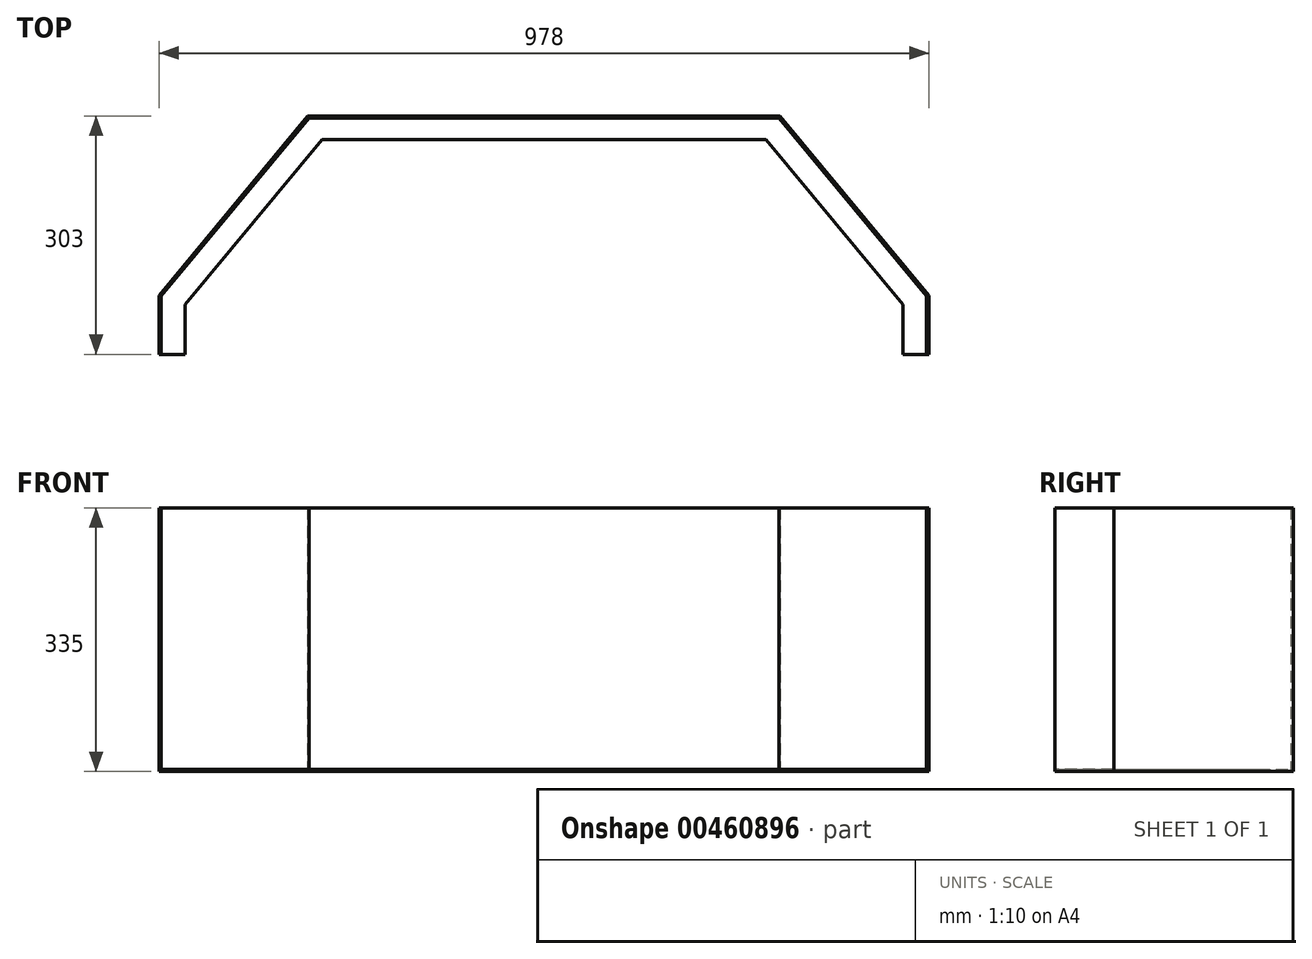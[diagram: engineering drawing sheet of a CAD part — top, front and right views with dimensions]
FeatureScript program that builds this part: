
annotation { "Feature Type Name" : "Feature", "Feature Type Description" : "" }
export const myFeature = defineFeature(function(context is Context, id is Id, definition is map)
    precondition{}
    {
        {
            var Q0;
            Q0=qCreatedBy(makeId("Top.planeOp"),FACE);
            var sketch = newSketch(context, id + "F0", { "sketchPlane" : qUnion([Q0])});
            skLineSegment(sketch, "E0", {"start": v(0, 0) * mm, "end": v(0, 75) * mm});
            skLineSegment(sketch, "E1", {"start": v(0, 75) * mm, "end": v(189, 303) * mm});
            skLineSegment(sketch, "E2", {"start": v(189, 303) * mm, "end": v(789, 303) * mm});
            skLineSegment(sketch, "E3", {"start": v(789, 303) * mm, "end": v(978, 75) * mm});
            skLineSegment(sketch, "E4", {"start": v(978, 75) * mm, "end": v(978, 0) * mm});
            skLineSegment(sketch, "E5", {"start": v(0, 0) * mm, "end": v(33, 0) * mm});
            skLineSegment(sketch, "E6", {"start": v(33, 0) * mm, "end": v(33, 63.1) * mm});
            skLineSegment(sketch, "E7", {"start": v(33, 63.1) * mm, "end": v(207, 273) * mm});
            skLineSegment(sketch, "E8", {"start": v(207, 273) * mm, "end": v(771, 273) * mm});
            skLineSegment(sketch, "E9", {"start": v(771, 273) * mm, "end": v(945, 63.1) * mm});
            skLineSegment(sketch, "E10", {"start": v(945, 63.1) * mm, "end": v(945, 0) * mm});
            skLineSegment(sketch, "E11", {"start": v(945, 0) * mm, "end": v(978, 0) * mm});
            skLineSegment(sketch, "E12", {"start": v(3, 0) * mm, "end": v(3, 73.92) * mm});
            skLineSegment(sketch, "E13", {"start": v(3, 73.92) * mm, "end": v(190.4, 300) * mm});
            skLineSegment(sketch, "E14", {"start": v(190.4, 300) * mm, "end": v(787.6, 300) * mm});
            skLineSegment(sketch, "E15", {"start": v(973.8, 0) * mm, "end": v(978, 0) * mm});
            skLineSegment(sketch, "E16", {"start": v(787.6, 300) * mm, "end": v(975, 73.92) * mm});
            skLineSegment(sketch, "E17", {"start": v(975, 73.92) * mm, "end": v(975, 0) * mm});
            skSolve(sketch);
        }
        {
            var Q0;
            {var subQ4=sQuery(id+"F0.wireOp",EDGE,"E0");Q0=makeQuery(id+"F0.imprint","IMPRINT",FACE,{"disambiguationData":[TD([[makeQuery(id+"F0.imprint","IMPRINT",EDGE,{"derivedFrom":subQ4}),-1.0]])]});}
            extrude(context, id + "F1", {"entities" : qUnion([Q0]), "depth" : 335 * mm});
        }
        {
            var Q0;
            {var subQ2=sQuery(id+"F0.wireOp",EDGE,"E6");Q0=makeQuery(id+"F0.imprint","IMPRINT",FACE,{"disambiguationData":[TD([[makeQuery(id+"F0.imprint","IMPRINT",EDGE,{"derivedFrom":subQ2}),1.0]])]});}
            extrude(context, id + "F2", {"entities" : qUnion([Q0]), "operationType" : NewBodyOperationType.ADD, "depth" : 3 * mm});
        }
    });
